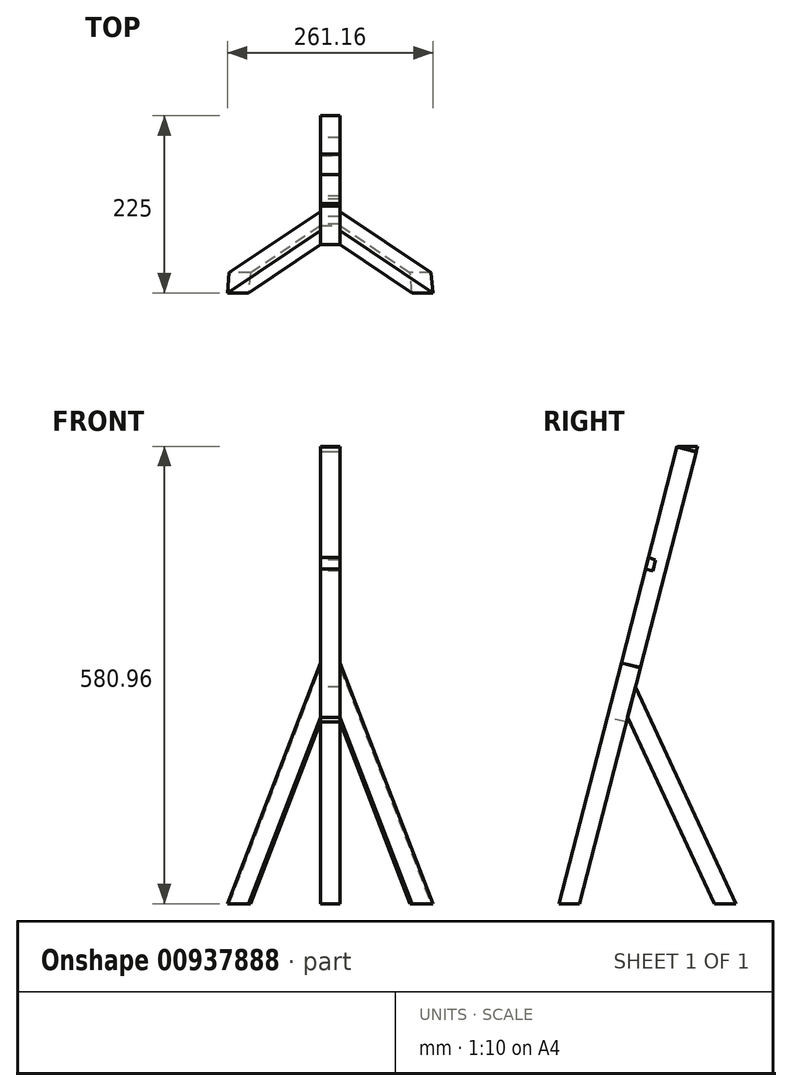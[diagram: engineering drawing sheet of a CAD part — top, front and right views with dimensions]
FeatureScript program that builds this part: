
annotation { "Feature Type Name" : "Feature", "Feature Type Description" : "" }
export const myFeature = defineFeature(function(context is Context, id is Id, definition is map)
    precondition{}
    {
        {
            var Q0;
            Q0=qCreatedBy(makeId("Right.planeOp"),FACE);
            var sketch = newSketch(context, id + "F0", { "sketchPlane" : qUnion([Q0])});
            skLineSegment(sketch, "E0", {"start": v(0, 0) * mm, "end": v(-75, 0) * mm, "construction": true});
            skLineSegment(sketch, "E1", {"start": v(0, 0) * mm, "end": v(150, 0) * mm, "construction": true});
            skLineSegment(sketch, "E2", {"start": v(75, 0) * mm, "end": v(75, 580) * mm, "construction": true});
            skLineSegment(sketch, "E3", {"start": v(75, 580) * mm, "end": v(-75, 0) * mm, "construction": true});
            skLineSegment(sketch, "E4", {"start": v(0, 0) * mm, "end": v(-7.63, 260.5) * mm, "construction": true});
            skLineSegment(sketch, "E5", {"start": v(-7.63, 260.5) * mm, "end": v(150, 0) * mm, "construction": true});
            skLineSegment(sketch, "E6", {"start": v(5.51, 311.31) * mm, "end": v(1.97, 297.62) * mm});
            skLineSegment(sketch, "E7", {"start": v(1.97, 297.62) * mm, "end": v(13.27, 294.7) * mm});
            skLineSegment(sketch, "E8", {"start": v(-7.63, 260.5) * mm, "end": v(-13.9, 236.29) * mm, "construction": true});
            skLineSegment(sketch, "E9", {"start": v(38.75, 439.85) * mm, "end": v(35, 425.31) * mm});
            skLineSegment(sketch, "E10", {"start": v(35, 425.31) * mm, "end": v(44.34, 422.9) * mm});
            skLineSegment(sketch, "E11", {"start": v(44.34, 422.9) * mm, "end": v(47.85, 436.48) * mm});
            skLineSegment(sketch, "E12", {"start": v(47.85, 436.48) * mm, "end": v(38.75, 439.85) * mm});
            skLineSegment(sketch, "E13", {"start": v(75, 580) * mm, "end": v(155.18, 580) * mm, "construction": true});
            skLineSegment(sketch, "E14", {"start": v(75, 580) * mm, "end": v(99.2, 573.74) * mm});
            skLineSegment(sketch, "E15", {"start": v(99.2, 573.74) * mm, "end": v(100.82, 580) * mm});
            skLineSegment(sketch, "E16", {"start": v(100.82, 580) * mm, "end": v(75, 580) * mm});
            skLineSegment(sketch, "E17", {"start": v(75, 580) * mm, "end": v(75.25, 580.96) * mm});
            skLineSegment(sketch, "E18", {"start": v(75.25, 580.96) * mm, "end": v(101.07, 580.96) * mm});
            skLineSegment(sketch, "E19", {"start": v(101.07, 580.96) * mm, "end": v(100.82, 580) * mm});
            skLineSegment(sketch, "E20", {"start": v(-13.9, 236.29) * mm, "end": v(0, 232.7) * mm, "construction": true});
            skLineSegment(sketch, "E21", {"start": v(-13.9, 236.29) * mm, "end": v(10.4, 230) * mm, "construction": true});
            skLineSegment(sketch, "E22", {"start": v(10.4, 230) * mm, "end": v(22.13, 275.32) * mm});
            skLineSegment(sketch, "E23", {"start": v(22.13, 275.32) * mm, "end": v(150, 0) * mm});
            skLineSegment(sketch, "E24.0", {"start": v(-0.55, 264.79) * mm, "end": v(127.33, -10.53) * mm});
            skLineSegment(sketch, "E25", {"start": v(150, 0) * mm, "end": v(122.44, 0) * mm});
            skSolve(sketch);
        }
        {
            var Q0;
            Q0 = qSketchRegion(id + "F0", true);
            extrude(context, id + "F1", {"entities" : qUnion([Q0]), "endBound" : BoundingType.SYMMETRIC, "depth" : 25 * mm, "offsetDistance" : 25 * mm});
        }
        {
            var Q0;
            Q0=makeQuery(id+"F1.opExtrude","SWEPT_FACE",FACE,{"disambiguationData":[OSD([sQuery(id+"F0.wireOp",EDGE,"E6")])]});
            var Q1;
            Q1=makeQuery(id+"F1.opExtrude","SWEPT_FACE",FACE,{"disambiguationData":[OSD([sQuery(id+"F0.wireOp",EDGE,"E9")])]});
            cPlane(context, id + "F2", {"entities" : qUnion([Q0, Q1]), "cplaneType" : CPlaneType.OFFSET, "offset" : 0 * mm, "width" : 150 * mm, "height" : 150 * mm});
        }
        {
            var Q0;
            Q0=qCreatedBy(id+"F2.planeOp",FACE);
            var sketch = newSketch(context, id + "F3", { "sketchPlane" : qUnion([Q0])});
            skLineSegment(sketch, "E26", {"start": v(0, -19.06) * mm, "end": v(130, -19.06) * mm, "construction": true});
            skLineSegment(sketch, "E27", {"start": v(0, -19.06) * mm, "end": v(-130, -19.06) * mm, "construction": true});
            skLineSegment(sketch, "E28", {"start": v(0, -19.06) * mm, "end": v(0, 580.94) * mm, "construction": true});
            skLineSegment(sketch, "E29.0", {"start": v(12.5, -19.06) * mm, "end": v(12.5, 297.4) * mm});
            skLineSegment(sketch, "E30.0", {"start": v(-12.5, -19.06) * mm, "end": v(-12.5, 297.4) * mm});
            skLineSegment(sketch, "E31", {"start": v(0, -19.06) * mm, "end": v(0, 225.94) * mm, "construction": true});
            skLineSegment(sketch, "E32", {"start": v(-12.4, 225.94) * mm, "end": v(12.5, 225.94) * mm});
            skLineSegment(sketch, "E33", {"start": v(-12.5, 225.94) * mm, "end": v(-104, -19.06) * mm, "construction": true});
            skLineSegment(sketch, "E34.0", {"start": v(-35.92, 234.68) * mm, "end": v(-127.42, -10.32) * mm, "construction": true});
            skLineSegment(sketch, "E35", {"start": v(-35.92, 234.68) * mm, "end": v(-12.5, 297.4) * mm});
            skLineSegment(sketch, "E36", {"start": v(-12.5, 297.4) * mm, "end": v(-127.42, -10.32) * mm});
            skLineSegment(sketch, "E37", {"start": v(-130, -19.06) * mm, "end": v(-104, -19.06) * mm});
            skLineSegment(sketch, "E38", {"start": v(-104, -19.06) * mm, "end": v(-12.5, 225.94) * mm});
            skLineSegment(sketch, "E39", {"start": v(-130, -19.06) * mm, "end": v(-130.69, -19.06) * mm});
            skLineSegment(sketch, "E40", {"start": v(-127.42, -10.32) * mm, "end": v(-130.69, -19.06) * mm});
            skLineSegment(sketch, "E41.MirrorCS", {"start": v(35.92, 234.68) * mm, "end": v(127.42, -10.32) * mm, "construction": true});
            skLineSegment(sketch, "E42.MirrorCS", {"start": v(12.5, 297.4) * mm, "end": v(127.42, -10.32) * mm});
            skPoint(sketch, "E43.MirrorCS.end.orphan", {"position": v(104, -19.06) * mm});
            skPoint(sketch, "E43.MirrorCS.start.orphan", {"position": v(12.5, 225.94) * mm});
            skLineSegment(sketch, "E44", {"start": v(12.5, 225.94) * mm, "end": v(104, -19.06) * mm});
            skLineSegment(sketch, "E45", {"start": v(104, -19.06) * mm, "end": v(130.69, -19.06) * mm});
            skLineSegment(sketch, "E46", {"start": v(127.42, -10.32) * mm, "end": v(130.69, -19.06) * mm});
            skLineSegment(sketch, "E47", {"start": v(-12.5, 580.94) * mm, "end": v(12.5, 580.94) * mm});
            skLineSegment(sketch, "E48.left", {"start": v(-12.5, 297.4) * mm, "end": v(-12.5, 225.94) * mm});
            skLineSegment(sketch, "E48.right", {"start": v(-12.4, 297.4) * mm, "end": v(-12.4, 225.94) * mm});
            skLineSegment(sketch, "E49.top", {"start": v(12.5, 225.94) * mm, "end": v(12.4, 225.94) * mm});
            skLineSegment(sketch, "E49.left", {"start": v(12.5, 297.4) * mm, "end": v(12.5, 225.94) * mm});
            skLineSegment(sketch, "E49.right", {"start": v(12.4, 297.4) * mm, "end": v(12.4, 225.94) * mm});
            skLineSegment(sketch, "E50", {"start": v(-12.4, 297.4) * mm, "end": v(-12.4, 297.42) * mm});
            skLineSegment(sketch, "E51", {"start": v(-12.4, 297.42) * mm, "end": v(-12.5, 297.42) * mm});
            skLineSegment(sketch, "E52", {"start": v(-12.4, 225.94) * mm, "end": v(-12.4, 225.76) * mm});
            skLineSegment(sketch, "E53", {"start": v(-12.4, 225.76) * mm, "end": v(-12.5, 225.76) * mm});
            skLineSegment(sketch, "E54", {"start": v(-12.5, 225.76) * mm, "end": v(-12.5, 225.94) * mm});
            skLineSegment(sketch, "E55.trimOffspring", {"start": v(-12.5, 297.42) * mm, "end": v(-12.5, 580.94) * mm});
            skLineSegment(sketch, "E56", {"start": v(12.5, 297.45) * mm, "end": v(12.4, 297.45) * mm});
            skLineSegment(sketch, "E57", {"start": v(12.4, 297.45) * mm, "end": v(12.4, 297.4) * mm});
            skLineSegment(sketch, "E58.trimOffspring", {"start": v(12.5, 297.45) * mm, "end": v(12.5, 580.94) * mm});
            skSolve(sketch);
        }
        {
            var Q0;
            Q0 = qSketchRegion(id + "F3", true);
            extrude(context, id + "F4", {"entities" : qUnion([Q0]), "oppositeDirection" : true, "depth" : 25 * mm, "offsetDistance" : 25 * mm});
        }
        {
            var Q0;
            Q0=qCreatedBy(makeId("Right.planeOp"),FACE);
            var sketch = newSketch(context, id + "F5", { "sketchPlane" : qUnion([Q0])});
            skLineSegment(sketch, "E59", {"start": v(0, 0) * mm, "end": v(-124.74, 0) * mm});
            skLineSegment(sketch, "E60", {"start": v(-124.74, 0) * mm, "end": v(-124.74, -31.23) * mm});
            skLineSegment(sketch, "E61", {"start": v(-124.74, -31.23) * mm, "end": v(0, -31.23) * mm});
            skLineSegment(sketch, "E62", {"start": v(0, -31.23) * mm, "end": v(0, 0) * mm});
            skSolve(sketch);
        }
        {
            var Q0;
            Q0 = qSketchRegion(id + "F5", true);
            extrude(context, id + "F6", {"entities" : qUnion([Q0]), "operationType" : NewBodyOperationType.REMOVE, "endBound" : BoundingType.SYMMETRIC, "oppositeDirection" : true, "depth" : 288 * mm, "offsetDistance" : 25 * mm});
        }
        {
            var Q0;
            Q0 = qSketchRegion(id + "F5", true);
            extrude(context, id + "F7", {"entities" : qUnion([Q0]), "operationType" : NewBodyOperationType.REMOVE, "depth" : 286 * mm, "offsetDistance" : 25 * mm});
        }
        {
            var Q0;
            Q0 = qSketchRegion(id + "F0", true);
            extrude(context, id + "F8", {"entities" : qUnion([Q0]), "endBound" : BoundingType.SYMMETRIC, "depth" : 25 * mm, "offsetDistance" : 25 * mm});
        }
        {
            var Q0;
            Q0 = qSketchRegion(id + "F0", true);
            extrude(context, id + "F9", {"entities" : qUnion([Q0]), "endBound" : BoundingType.SYMMETRIC, "depth" : 25 * mm, "offsetDistance" : 25 * mm});
        }
    });
